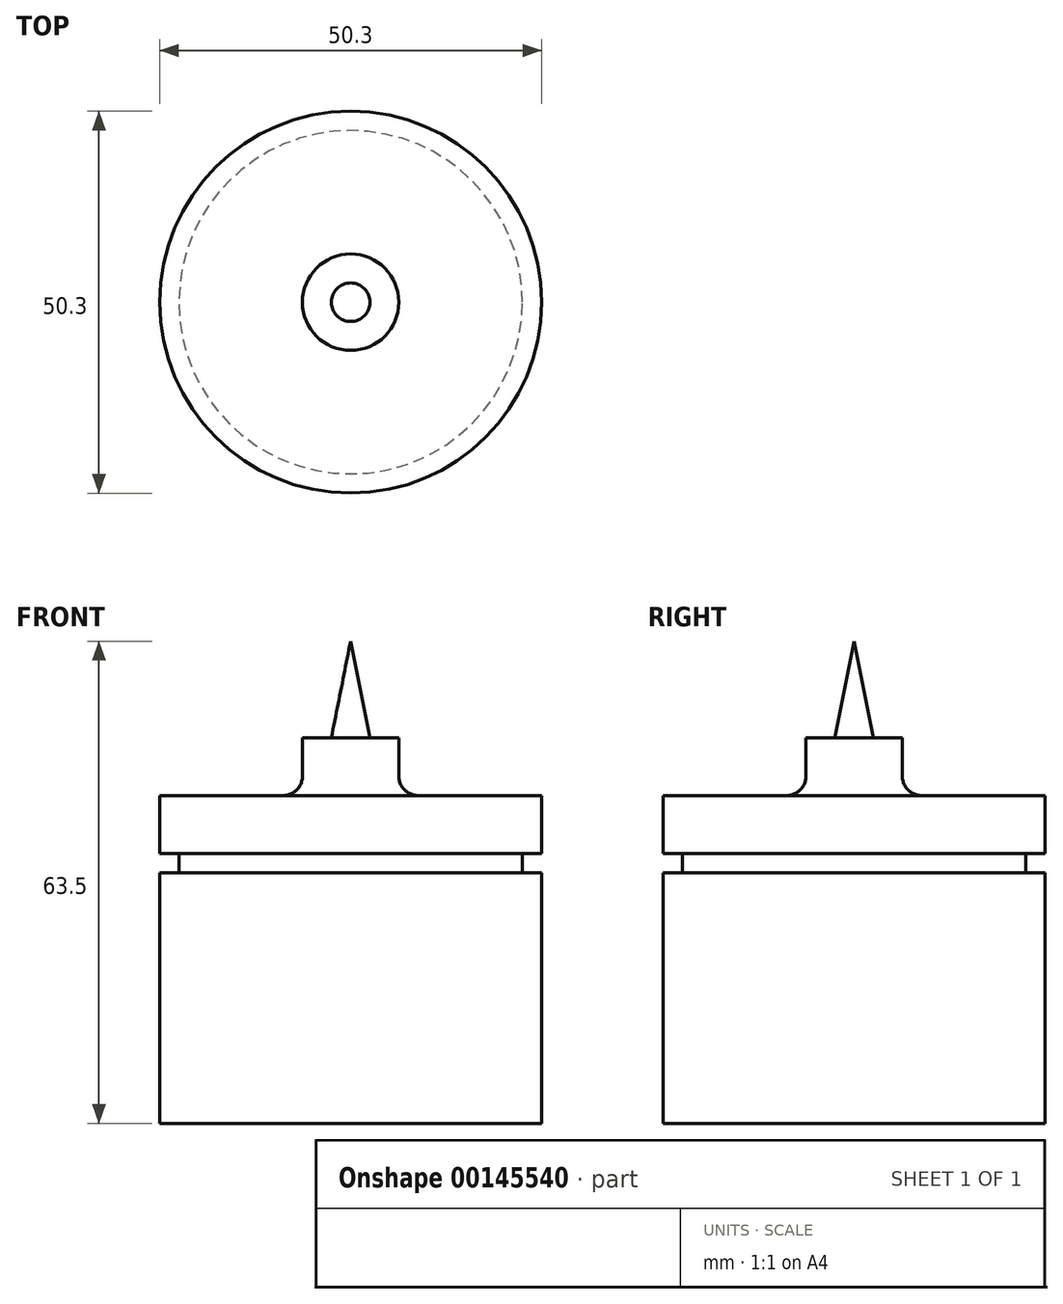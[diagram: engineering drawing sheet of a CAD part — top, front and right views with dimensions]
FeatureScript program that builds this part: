
annotation { "Feature Type Name" : "Feature", "Feature Type Description" : "" }
export const myFeature = defineFeature(function(context is Context, id is Id, definition is map)
    precondition{}
    {
        {
            var Q0;
            Q0=qCreatedBy(makeId("Front.planeOp"),FACE);
            var sketch = newSketch(context, id + "F0", { "sketchPlane" : qUnion([Q0])});
            skLineSegment(sketch, "E0.bottom", {"start": v(0, 0) * mm, "end": v(25.15, 0) * mm});
            skLineSegment(sketch, "E0.top", {"start": v(6.35, 43.18) * mm, "end": v(25.15, 43.18) * mm});
            skLineSegment(sketch, "E0.left", {"start": v(0, 0) * mm, "end": v(0, 43.18) * mm});
            skLineSegment(sketch, "E0.right", {"start": v(25.15, 0) * mm, "end": v(25.15, 33.02) * mm});
            skLineSegment(sketch, "E1.bottom", {"start": v(25.15, 35.56) * mm, "end": v(22.6, 35.56) * mm});
            skLineSegment(sketch, "E1.top", {"start": v(25.15, 33.02) * mm, "end": v(22.6, 33.02) * mm});
            skLineSegment(sketch, "E1.right", {"start": v(22.6, 35.56) * mm, "end": v(22.6, 33.02) * mm});
            skLineSegment(sketch, "E2.top", {"start": v(0, 50.8) * mm, "end": v(6.35, 50.8) * mm});
            skLineSegment(sketch, "E2.left", {"start": v(0, 43.18) * mm, "end": v(0, 50.8) * mm});
            skLineSegment(sketch, "E2.right", {"start": v(6.35, 43.18) * mm, "end": v(6.35, 50.8) * mm});
            skLineSegment(sketch, "E3.trimOffspring", {"start": v(25.15, 35.56) * mm, "end": v(25.15, 43.18) * mm});
            skLineSegment(sketch, "E4", {"start": v(3.18, 50.8) * mm, "end": v(0, 58.41) * mm});
            skLineSegment(sketch, "E5", {"start": v(0, 58.41) * mm, "end": v(0, 50.8) * mm});
            skSolve(sketch);
        }
        {
            var Q0;
            Q0=qCreatedBy(makeId("Front.planeOp"),FACE);
            var sketch = newSketch(context, id + "F1", { "sketchPlane" : qUnion([Q0])});
            skLineSegment(sketch, "E6", {"start": v(0, 0) * mm, "end": v(0, 40.64) * mm});
            skSolve(sketch);
        }
        {
            var Q0;
            Q0=makeQuery(id+"F0.imprint","IMPRINT",FACE,{"disambiguationData":[TD([[makeQuery(id+"F0.imprint","IMPRINT",EDGE,{"derivedFrom":sQuery(id+"F0.wireOp",EDGE,"E0.bottom")}),1.0]])]});
            var Q1;
            Q1=sQuery(id+"F1.wireOp",EDGE,"E6");
            revolve(context, id + "F2", {"entities" : qUnion([Q0]), "axis" : qUnion([Q1]), "revolveType" : RevolveType.FULL});
        }
        {
            var Q0;
            Q0=makeQuery(id+"F2.opRevolve","SWEPT_EDGE",EDGE,{"disambiguationData":[OSD([sQuery(id+"F0.wireOp",EDGE,"E0.top"),sQuery(id+"F0.wireOp",EDGE,"E2.right")])]});
            fillet(context, id + "F3", {"entities" : qUnion([Q0]), "radius" : 2.54 * mm, "tangentPropagation" : true, "allowEdgeOverflow" : false});
        }
        {
            var Q0;
            Q0=qCreatedBy(makeId("Front.planeOp"),FACE);
            var sketch = newSketch(context, id + "F4", { "sketchPlane" : qUnion([Q0])});
            skLineSegment(sketch, "E7", {"start": v(2.54, 50.8) * mm, "end": v(0, 63.5) * mm});
            skLineSegment(sketch, "E8", {"start": v(0, 63.5) * mm, "end": v(0, 50.8) * mm});
            skLineSegment(sketch, "E9", {"start": v(0, 50.8) * mm, "end": v(2.54, 50.8) * mm});
            skSolve(sketch);
        }
        {
            var Q0;
            Q0=qCreatedBy(makeId("Front.planeOp"),FACE);
            var sketch = newSketch(context, id + "F5", { "sketchPlane" : qUnion([Q0])});
            skLineSegment(sketch, "E10", {"start": v(0, 63.5) * mm, "end": v(0, 50.8) * mm});
            skSolve(sketch);
        }
        {
            var Q0;
            Q0=makeQuery(id+"F4.imprint","IMPRINT",FACE,{"disambiguationData":[TD([[makeQuery(id+"F4.imprint","IMPRINT",EDGE,{"derivedFrom":sQuery(id+"F4.wireOp",EDGE,"E7")}),1.0]])]});
            var Q1;
            Q1=sQuery(id+"F5.wireOp",EDGE,"E10");
            revolve(context, id + "F6", {"entities" : qUnion([Q0]), "axis" : qUnion([Q1]), "revolveType" : RevolveType.FULL});
        }
    });
